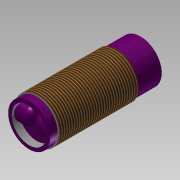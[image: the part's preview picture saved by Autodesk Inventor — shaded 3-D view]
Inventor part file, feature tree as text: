
AUTODESK INVENTOR PART (.ipt)
format: ipt  version: 2015 SP1 (Build 190203100, 203)  size: 189,440 bytes
history: native  units: mm
features: extrude x7, sketch x7, fillet x2, thread x1, projected_geometry x1
ambient origin geometry x8: Origin, YZ Plane, XZ Plane, XY Plane, X Axis, Y Axis, Z Axis, Center Point
bodies: Solid1 (feature_tree)
feature tree (18):
  extrude  "Extrusion1"  Depth=31.82mm TaperAngle=0.0deg
  thread  "Thread1"  [1 undecoded]
  extrude  "Extrusion2"  Depth=1.4mm
  extrude  "Extrusion3"  Depth=3.0mm TaperAngle=0.0deg
  fillet  "Fillet1"  Radius=3.0mm
  fillet  "Fillet2"  Radius=3.0mm
  extrude  "Extrusion4"  Depth=9.6mm TaperAngle=0.0deg
  sketch  "Sketch5"  dims[d22=3.0mm d23=6.71mm]
  extrude  "Extrusion5"  Depth=3.0mm
  extrude  "Extrusion6"  Depth=4.1mm TaperAngle=0.0deg
  sketch  "Sketch6"  dims[d24=1.0mm d25=0.0mm d26=4.1mm d27=0.0mm]
  extrude  "Extrusion7"  [1 undecoded]
  sketch  "Sketch1"  dims[d0=17.8mm d1=31.82mm d2=0.0mm d3=10.0mm d4=0.0mm]
  sketch  "Sketch2"  dims[d5=16.74mm d6=1.4mm]
  sketch  "Sketch3"  dims[d7=3.0mm d8=0.0mm d15=2.0mm d16=0.0mm d17=3.0mm d18=3.0mm]
  sketch  "Sketch4"  dims[d19=16.89mm d20=9.6mm d21=0.0mm]
  sketch  "Sketch7"  dims[d28=200.0mm d29=0.0mm]
  projected_geometry  "Projected Loop2"
note: 2 required parameter values undecoded (feature->parameter linkage not recoverable at this tier; creation-order binding heuristic only, values carry confidence <= 0.55)
